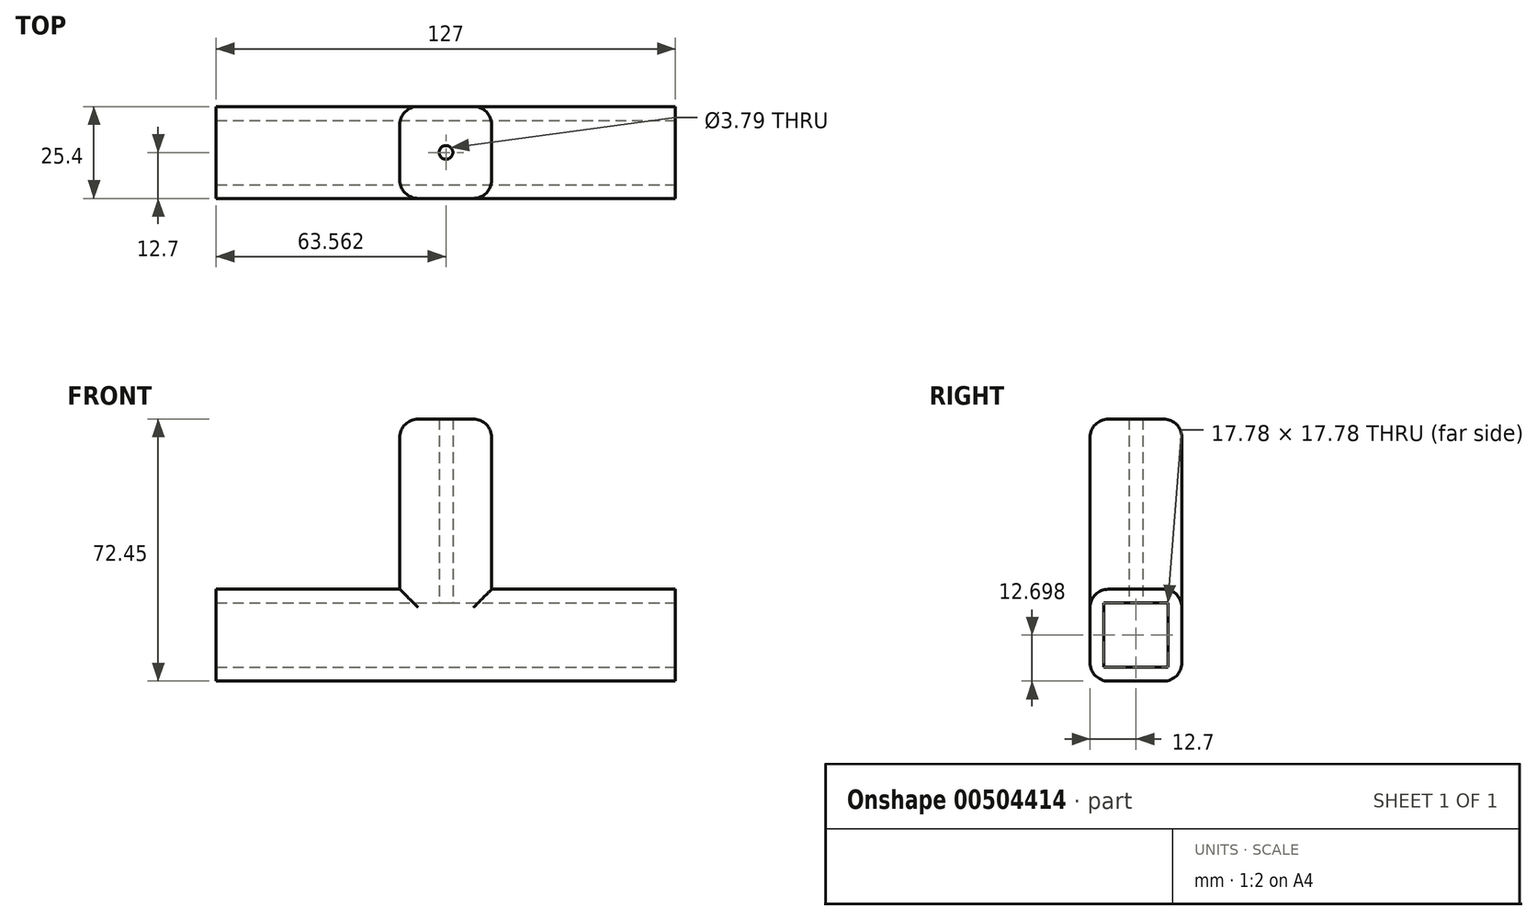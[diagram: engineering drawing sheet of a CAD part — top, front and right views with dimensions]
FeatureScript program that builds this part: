
annotation { "Feature Type Name" : "Feature", "Feature Type Description" : "" }
export const myFeature = defineFeature(function(context is Context, id is Id, definition is map)
    precondition{}
    {
        {
            var Q0;
            Q0=qCreatedBy(makeId("Front.planeOp"),FACE);
            var sketch = newSketch(context, id + "F0", { "sketchPlane" : qUnion([Q0])});
            skLineSegment(sketch, "E0.bottom", {"start": v(-61.03, -32.6) * mm, "end": v(65.97, -32.6) * mm});
            skLineSegment(sketch, "E0.top", {"start": v(-61.03, -7.2) * mm, "end": v(65.97, -7.2) * mm});
            skLineSegment(sketch, "E0.left", {"start": v(-61.03, -32.6) * mm, "end": v(-61.03, -7.2) * mm});
            skLineSegment(sketch, "E0.right", {"start": v(65.97, -32.6) * mm, "end": v(65.97, -7.2) * mm});
            skLineSegment(sketch, "E1.bottom", {"start": v(-10.23, 39.85) * mm, "end": v(15.17, 39.85) * mm});
            skLineSegment(sketch, "E1.left", {"start": v(-10.23, 39.85) * mm, "end": v(-10.23, -7.2) * mm});
            skLineSegment(sketch, "E1.right", {"start": v(15.17, 39.85) * mm, "end": v(15.17, -7.2) * mm});
            skSolve(sketch);
        }
        {
            var Q0;
            Q0=makeQuery(id+"F0.imprint","IMPRINT",FACE,{"disambiguationData":[TD([[makeQuery(id+"F0.imprint","IMPRINT",EDGE,{"derivedFrom":sQuery(id+"F0.wireOp",EDGE,"E1.bottom")}),-1.0]])]});
            var Q1;
            Q1=makeQuery(id+"F0.imprint","IMPRINT",FACE,{"disambiguationData":[TD([[makeQuery(id+"F0.imprint","IMPRINT",EDGE,{"derivedFrom":sQuery(id+"F0.wireOp",EDGE,"E0.bottom")}),1.0]])]});
            extrude(context, id + "F1", {"entities" : qUnion([Q0, Q1]), "endBound" : BoundingType.SYMMETRIC, "depth" : 25.4 * mm});
        }
        {
            var Q0;
            Q0=makeQuery(id+"F1.opExtrude","SWEPT_FACE",FACE,{"disambiguationData":[OSD([sQuery(id+"F0.wireOp",EDGE,"E0.right")])]});
            var sketch = newSketch(context, id + "F2", { "sketchPlane" : qUnion([Q0])});
            skLineSegment(sketch, "E2.0", {"start": v(-8.9, -11.01) * mm, "end": v(8.9, -11.01) * mm});
            skLineSegment(sketch, "E2.1", {"start": v(-8.9, -28.8) * mm, "end": v(-8.9, -11.01) * mm});
            skLineSegment(sketch, "E2.2", {"start": v(-8.9, -28.8) * mm, "end": v(8.9, -28.8) * mm});
            skLineSegment(sketch, "E2.3", {"start": v(8.9, -28.8) * mm, "end": v(8.9, -11.01) * mm});
            skSolve(sketch);
        }
        {
            var Q0;
            Q0=makeQuery(id+"F2.imprint","IMPRINT",FACE,{"disambiguationData":[TD([[makeQuery(id+"F2.imprint","IMPRINT",EDGE,{"derivedFrom":sQuery(id+"F2.wireOp",EDGE,"E2.0")}),-1.0]])]});
            extrude(context, id + "F3", {"entities" : qUnion([Q0]), "operationType" : NewBodyOperationType.REMOVE, "endBound" : BoundingType.SYMMETRIC, "oppositeDirection" : true, "depth" : 480.06 * mm});
        }
        {
            var Q0;
            Q0=makeQuery(id+"F1.opExtrude","SWEPT_FACE",FACE,{"disambiguationData":[OSD([sQuery(id+"F0.wireOp",EDGE,"E1.bottom")])]});
            var sketch = newSketch(context, id + "F4", { "sketchPlane" : qUnion([Q0])});
            skCircle(sketch, "E3", {"center": v(2.53, 0) * mm, "radius": 1.9 * mm});
            skSolve(sketch);
        }
        {
            var Q0;
            Q0=makeQuery(id+"F4.imprint","IMPRINT",FACE,{"disambiguationData":[TD([[makeQuery(id+"F4.imprint","IMPRINT",EDGE,{"derivedFrom":sQuery(id+"F4.wireOp",EDGE,"E3")}),1.0]])]});
            extrude(context, id + "F5", {"entities" : qUnion([Q0]), "operationType" : NewBodyOperationType.REMOVE, "endBound" : BoundingType.SYMMETRIC, "depth" : -127 * mm});
        }
        {
            var Q0;
            {var subQ0=sQuery(id+"F0.wireOp",EDGE,"E0.top");Q0=makeQuery(id+"F1.opExtrude","CAP_EDGE",EDGE,{"disambiguationData":[OSD([subQ0]),TDD([makeQuery(id+"F0.imprint","IMPRINT",EDGE,{"disambiguationData":[TD([[makeQuery(id+"F0.imprint","INTERSECT",VERTEX,{"derivedFrom":[subQ0,sQuery(id+"F0.wireOp",EDGE,"E0.right")]}),1.0]])],"derivedFrom":subQ0})])],"isStart":false});}
            var Q1;
            {var subQ0=sQuery(id+"F0.wireOp",EDGE,"E0.top");Q1=makeQuery(id+"F1.opExtrude","CAP_EDGE",EDGE,{"disambiguationData":[OSD([subQ0]),TDD([makeQuery(id+"F0.imprint","IMPRINT",EDGE,{"disambiguationData":[TD([[makeQuery(id+"F0.imprint","INTERSECT",VERTEX,{"derivedFrom":[subQ0,sQuery(id+"F0.wireOp",EDGE,"E0.right")]}),1.0]])],"derivedFrom":subQ0})])],"isStart":true});}
            var Q2;
            {var subQ0=sQuery(id+"F0.wireOp",EDGE,"E0.top");Q2=makeQuery(id+"F1.opExtrude","CAP_EDGE",EDGE,{"disambiguationData":[OSD([subQ0]),TDD([makeQuery(id+"F0.imprint","IMPRINT",EDGE,{"disambiguationData":[TD([[makeQuery(id+"F0.imprint","INTERSECT",VERTEX,{"derivedFrom":[subQ0,sQuery(id+"F0.wireOp",EDGE,"E0.left")]}),-1.0]])],"derivedFrom":subQ0})])],"isStart":false});}
            var Q3;
            {var subQ0=sQuery(id+"F0.wireOp",EDGE,"E0.top");Q3=makeQuery(id+"F1.opExtrude","CAP_EDGE",EDGE,{"disambiguationData":[OSD([subQ0]),TDD([makeQuery(id+"F0.imprint","IMPRINT",EDGE,{"disambiguationData":[TD([[makeQuery(id+"F0.imprint","INTERSECT",VERTEX,{"derivedFrom":[subQ0,sQuery(id+"F0.wireOp",EDGE,"E0.left")]}),-1.0]])],"derivedFrom":subQ0})])],"isStart":true});}
            var Q4;
            Q4=makeQuery(id+"F1.opExtrude","CAP_EDGE",EDGE,{"disambiguationData":[OSD([sQuery(id+"F0.wireOp",EDGE,"E0.bottom")])],"isStart":false});
            var Q5;
            Q5=makeQuery(id+"F1.opExtrude","CAP_EDGE",EDGE,{"disambiguationData":[OSD([sQuery(id+"F0.wireOp",EDGE,"E0.bottom")])],"isStart":true});
            var Q6;
            Q6=makeQuery(id+"F1.opExtrude","CAP_EDGE",EDGE,{"disambiguationData":[OSD([sQuery(id+"F0.wireOp",EDGE,"E1.right")])],"isStart":false});
            var Q7;
            Q7=makeQuery(id+"F1.opExtrude","CAP_EDGE",EDGE,{"disambiguationData":[OSD([sQuery(id+"F0.wireOp",EDGE,"E1.left")])],"isStart":false});
            var Q8;
            Q8=makeQuery(id+"F1.opExtrude","CAP_EDGE",EDGE,{"disambiguationData":[OSD([sQuery(id+"F0.wireOp",EDGE,"E1.left")])],"isStart":true});
            var Q9;
            Q9=makeQuery(id+"F1.opExtrude","CAP_EDGE",EDGE,{"disambiguationData":[OSD([sQuery(id+"F0.wireOp",EDGE,"E1.right")])],"isStart":true});
            var Q10;
            Q10=makeQuery(id+"F1.opExtrude","CAP_EDGE",EDGE,{"disambiguationData":[OSD([sQuery(id+"F0.wireOp",EDGE,"E1.bottom")])],"isStart":true});
            var Q11;
            Q11=makeQuery(id+"F1.opExtrude","SWEPT_EDGE",EDGE,{"disambiguationData":[OSD([sQuery(id+"F0.wireOp",EDGE,"E1.bottom"),sQuery(id+"F0.wireOp",EDGE,"E1.right")])]});
            var Q12;
            Q12=makeQuery(id+"F1.opExtrude","CAP_EDGE",EDGE,{"disambiguationData":[OSD([sQuery(id+"F0.wireOp",EDGE,"E1.bottom")])],"isStart":false});
            var Q13;
            Q13=makeQuery(id+"F1.opExtrude","SWEPT_EDGE",EDGE,{"disambiguationData":[OSD([sQuery(id+"F0.wireOp",EDGE,"E1.bottom"),sQuery(id+"F0.wireOp",EDGE,"E1.left")])]});
            fillet(context, id + "F6", {"entities" : qUnion([Q0, Q1, Q2, Q3, Q4, Q5, Q6, Q7, Q8, Q9, Q10, Q11, Q12, Q13]), "radius" : 5.08 * mm, "tangentPropagation" : true, "allowEdgeOverflow" : false});
        }
    });
